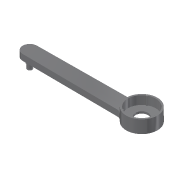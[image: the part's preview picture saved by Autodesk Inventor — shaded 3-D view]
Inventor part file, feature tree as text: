
AUTODESK INVENTOR PART (.ipt)
format: ipt  version: 2020 (Build 240168000, 168)  size: 437,248 bytes
history: native  units: mm (DEFAULTED — no unit token found)
features: other x12, extrude x10, sketch x9, fillet x3, pattern_circular x1, hole x1
bodies: Solide1 (feature_tree)
feature tree (36):
  other  "Origine"
  sketch  "Esquisse1"
  extrude  "Extrusion7"  Depth=78.0mm
  extrude  "Extrusion9"  Depth=20.0mm
  other  "Plan de construction2"
  sketch  "Esquisse13"
  extrude  "Extrusion19"  Depth=4.0mm TaperAngle=0.0deg
  extrude  "Extrusion20"  Depth=18.0mm
  extrude  "Extrusion21"  Depth=4.0mm
  other  "Plan de construction3"
  sketch  "Esquisse21"
  extrude  "Extrusion22"  Depth=4.0mm TaperAngle=0.0deg
  other  "Axe de construction2"
  pattern_circular  "Réseau circulaire1"  [2 undecoded]
  extrude  "Extrusion23"  Depth=50.0mm
  sketch  "Esquisse22"
  extrude  "Extrusion24"  Depth=1.5mm
  extrude  "Extrusion25"  Depth=1.5mm
  other  "Plan de construction4"
  extrude  "Extrusion26"  Depth=1.5mm
  fillet  "Congé12"  Radius=1.5mm
  fillet  "Congé13"  Radius=31.0mm
  hole  "Perçage6"  [1 undecoded]
  fillet  "Congé14"  Radius=3.0mm
  other  "Plan YZ"
  other  "Plan XZ"
  other  "Plan XY"
  other  "Axe X"
  other  "Axe Y"
  other  "Axe Z"
  other  "Point de centre"
  sketch  "Esquisse7"
  sketch  "Esquisse18"
  sketch  "Esquisse20"
  sketch  "Esquisse23"
  sketch  "Esquisse24"
note: 3 required parameter values undecoded (feature->parameter linkage not recoverable at this tier; creation-order binding heuristic only, values carry confidence <= 0.55)
